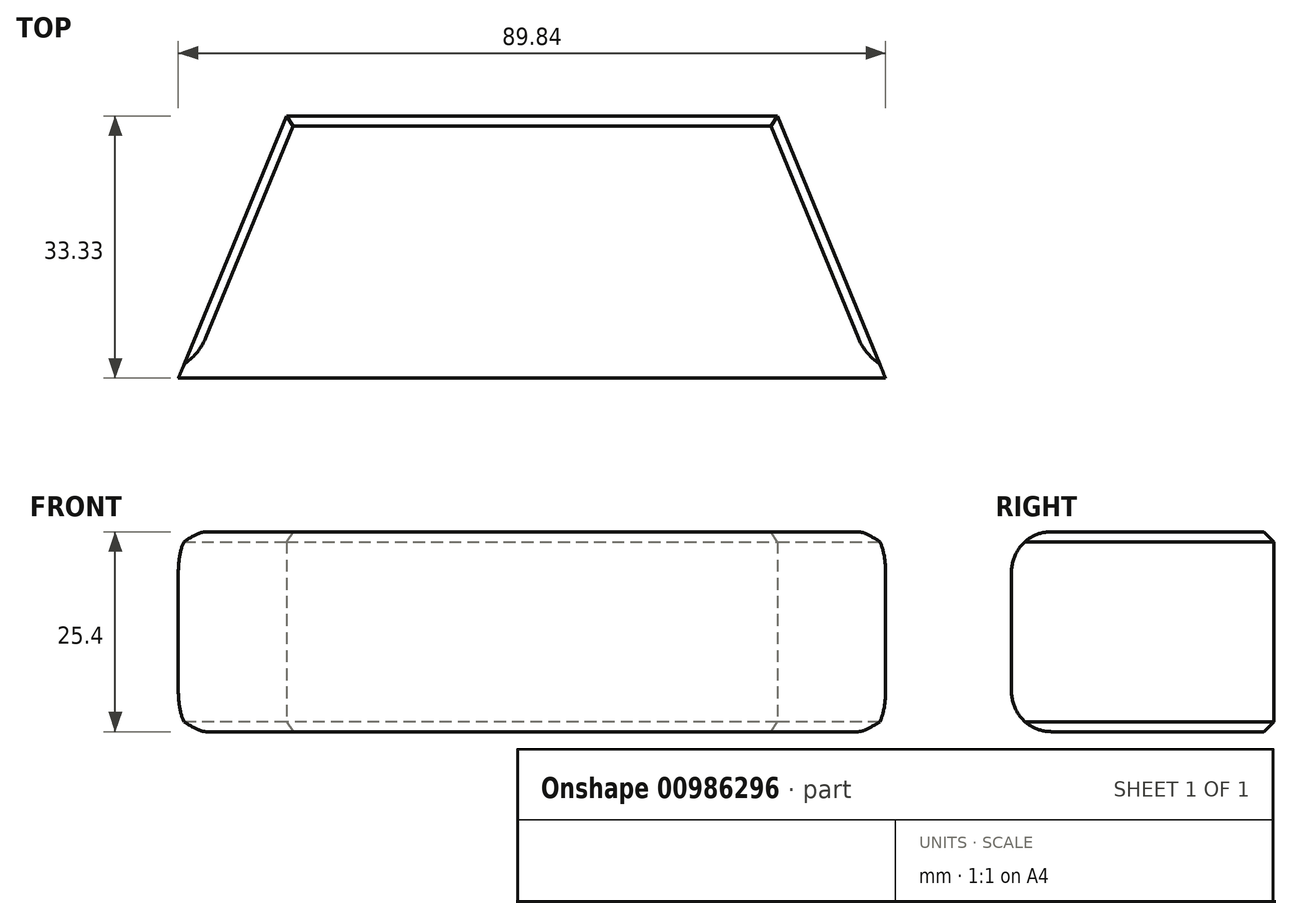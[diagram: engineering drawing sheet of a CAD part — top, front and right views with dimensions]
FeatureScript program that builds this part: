
annotation { "Feature Type Name" : "Feature", "Feature Type Description" : "" }
export const myFeature = defineFeature(function(context is Context, id is Id, definition is map)
    precondition{}
    {
        {
            var Q0;
            Q0=qCreatedBy(makeId("Top.planeOp"),FACE);
            var sketch = newSketch(context, id + "F0", { "sketchPlane" : qUnion([Q0])});
            skLineSegment(sketch, "E0", {"start": v(0, 0) * mm, "end": v(13.73, 33.33) * mm});
            skLineSegment(sketch, "E1", {"start": v(13.73, 33.33) * mm, "end": v(76.11, 33.33) * mm});
            skLineSegment(sketch, "E2", {"start": v(76.11, 33.33) * mm, "end": v(89.84, 0) * mm});
            skLineSegment(sketch, "E3", {"start": v(89.84, 0) * mm, "end": v(0, 0) * mm});
            skLineSegment(sketch, "E4", {"start": v(44.92, 33.33) * mm, "end": v(44.92, 0) * mm, "construction": true});
            skSolve(sketch);
        }
        {
            var Q0;
            Q0 = qSketchRegion(id + "F0", true);
            extrude(context, id + "F1", {"entities" : qUnion([Q0]), "depth" : 25.4 * mm, "offsetDistance" : 25.4 * mm});
        }
        {
            var Q0;
            Q0=makeQuery(id+"F1.opExtrude","CAP_EDGE",EDGE,{"disambiguationData":[OSD([sQuery(id+"F0.wireOp",EDGE,"E0")])],"isStart":false});
            var Q1;
            Q1=makeQuery(id+"F1.opExtrude","CAP_EDGE",EDGE,{"disambiguationData":[OSD([sQuery(id+"F0.wireOp",EDGE,"E0")])],"isStart":true});
            var Q2;
            Q2=makeQuery(id+"F1.opExtrude","CAP_EDGE",EDGE,{"disambiguationData":[OSD([sQuery(id+"F0.wireOp",EDGE,"E2")])],"isStart":false});
            var Q3;
            Q3=makeQuery(id+"F1.opExtrude","CAP_EDGE",EDGE,{"disambiguationData":[OSD([sQuery(id+"F0.wireOp",EDGE,"E2")])],"isStart":true});
            chamfer(context, id + "F2", {"entities" : qUnion([Q0, Q1, Q2, Q3]), "width" : 1.27 * mm, "tangentPropagation" : true});
        }
        {
            var Q0;
            Q0=makeQuery(id+"F1.opExtrude","CAP_EDGE",EDGE,{"disambiguationData":[OSD([sQuery(id+"F0.wireOp",EDGE,"E3")])],"isStart":true});
            var Q1;
            Q1=makeQuery(id+"F1.opExtrude","CAP_EDGE",EDGE,{"disambiguationData":[OSD([sQuery(id+"F0.wireOp",EDGE,"E3")])],"isStart":false});
            fillet(context, id + "F3", {"entities" : qUnion([Q0, Q1]), "radius" : 5.08 * mm, "tangentPropagation" : true, "allowEdgeOverflow" : false});
        }
        {
            var Q0;
            Q0=makeQuery(id+"F1.opExtrude","CAP_EDGE",EDGE,{"disambiguationData":[OSD([sQuery(id+"F0.wireOp",EDGE,"E1")])],"isStart":false});
            var Q1;
            Q1=makeQuery(id+"F1.opExtrude","CAP_EDGE",EDGE,{"disambiguationData":[OSD([sQuery(id+"F0.wireOp",EDGE,"E1")])],"isStart":true});
            chamfer(context, id + "F4", {"entities" : qUnion([Q0, Q1]), "width" : 1.27 * mm, "tangentPropagation" : true});
        }
    });
